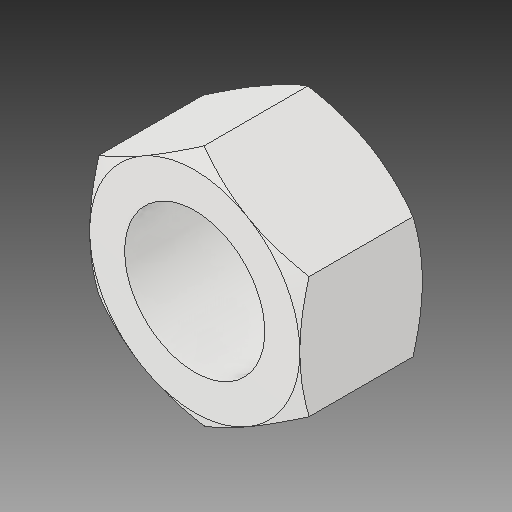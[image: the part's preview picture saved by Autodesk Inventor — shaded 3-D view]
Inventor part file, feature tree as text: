
AUTODESK INVENTOR PART (.ipt)
format: ipt  version: 2018 (Build 220112000, 112)  size: 121,856 bytes
history: native  units: in
note: dims shown in document units (in); Inventor stores cm internally (conversion verified against a paired STEP export)
features: mirror x1
ambient origin geometry x8: Origin, YZ Plane, XZ Plane, XY Plane, X Axis, Y Axis, Z Axis, Center Point
bodies: Solid1 (feature_tree)
feature tree (1):
  mirror  "Mirror1"
